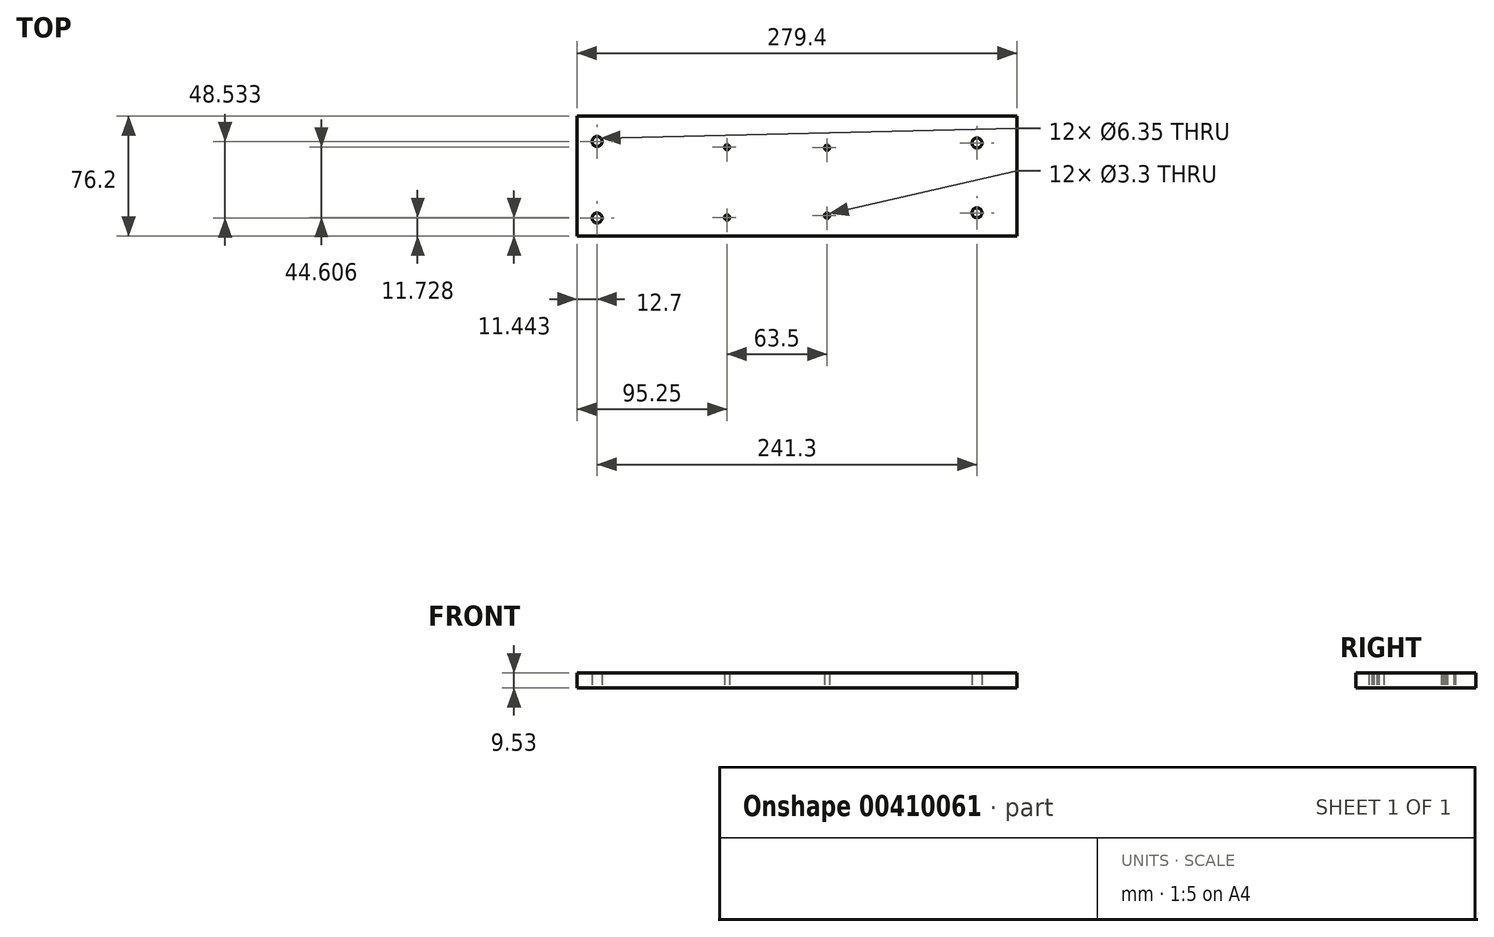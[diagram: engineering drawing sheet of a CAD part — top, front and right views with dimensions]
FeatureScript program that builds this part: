
annotation { "Feature Type Name" : "Feature", "Feature Type Description" : "" }
export const myFeature = defineFeature(function(context is Context, id is Id, definition is map)
    precondition{}
    {
        {
            var Q0;
            Q0=qCreatedBy(makeId("Top.planeOp"),FACE);
            var sketch = newSketch(context, id + "F0", { "sketchPlane" : qUnion([Q0])});
            skLineSegment(sketch, "E0.bottom", {"start": v(0, 0) * mm, "end": v(279.4, 0) * mm});
            skLineSegment(sketch, "E0.top", {"start": v(0, 76.2) * mm, "end": v(279.4, 76.2) * mm});
            skLineSegment(sketch, "E0.left", {"start": v(0, 0) * mm, "end": v(0, 76.2) * mm});
            skLineSegment(sketch, "E0.right", {"start": v(279.4, 0) * mm, "end": v(279.4, 76.2) * mm});
            skLineSegment(sketch, "E1", {"start": v(-52.08, 38.1) * mm, "end": v(340.24, 38.1) * mm, "construction": true});
            skCircle(sketch, "E2", {"center": v(12.7, 59.98) * mm, "radius": 3.18 * mm});
            skCircle(sketch, "E3", {"center": v(12.7, 11.44) * mm, "radius": 3.18 * mm});
            skCircle(sketch, "E4", {"center": v(95.25, 56.33) * mm, "radius": 1.65 * mm});
            skCircle(sketch, "E5", {"center": v(95.25, 11.73) * mm, "radius": 1.65 * mm});
            skCircle(sketch, "E6", {"center": v(158.75, 56.03) * mm, "radius": 1.65 * mm});
            skCircle(sketch, "E7", {"center": v(158.75, 12.95) * mm, "radius": 1.65 * mm});
            skCircle(sketch, "E8", {"center": v(254, 59.07) * mm, "radius": 3.18 * mm});
            skCircle(sketch, "E9", {"center": v(254, 14.72) * mm, "radius": 3.18 * mm});
            skSolve(sketch);
        }
        {
            var Q0;
            Q0=makeQuery(id+"F0.imprint","IMPRINT",FACE,{"disambiguationData":[TD([[makeQuery(id+"F0.imprint","IMPRINT",EDGE,{"derivedFrom":sQuery(id+"F0.wireOp",EDGE,"E0.bottom")}),1.0]])]});
            extrude(context, id + "F1", {"entities" : qUnion([Q0]), "depth" : 9.52 * mm});
        }
    });
